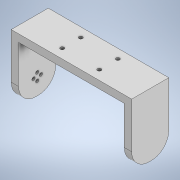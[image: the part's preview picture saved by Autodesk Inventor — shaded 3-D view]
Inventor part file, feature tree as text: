
AUTODESK INVENTOR PART (.ipt)
format: ipt  version: 2022 (Build 260153000, 153)  size: 164,864 bytes
history: native  units: mm
features: extrude x6, sketch x6, fillet x1
ambient origin geometry x8: Origin, YZ Plane, XZ Plane, XY Plane, X Axis, Y Axis, Z Axis, Center Point
bodies: Solid1 (feature_tree)
feature tree (13):
  extrude  "Extrusion1"  Depth=40.0mm
  extrude  "Extrusion3"  Depth=8.0mm
  extrude  "Extrusion4"  TaperAngle=0.0deg  [1 undecoded]
  extrude  "Extrusion6"  Depth=18.0mm
  fillet  "Fillet1"  Radius=3.5mm
  extrude  "Extrusion7"  Depth=8.0mm TaperAngle=0.0deg
  extrude  "Extrusion8"  Depth=15.0mm
  sketch  "Sketch1"  dims[d0=130.0mm d1=40.0mm]
  sketch  "Sketch3"  dims[d2=50.0mm d3=0.0mm d8=8.0mm]
  sketch  "Sketch4"  dims[d9=42.0mm d10=0.0mm d11=0.0mm]
  sketch  "Sketch7"  dims[d12=18.0mm d13=0.0mm d23=18.0mm d25=3.5mm]
  sketch  "Sketch8"  dims[d26=40.0mm d28=360.0deg d30=8.0mm d31=0.0mm]
  sketch  "Sketch9"  dims[d32=18.75mm d33=12.8mm d34=15.0mm d35=0.0mm d40=4.0mm d41=0.0mm d42=0.0mm]
note: 1 required parameter value undecoded (feature->parameter linkage not recoverable at this tier; creation-order binding heuristic only, values carry confidence <= 0.55)
